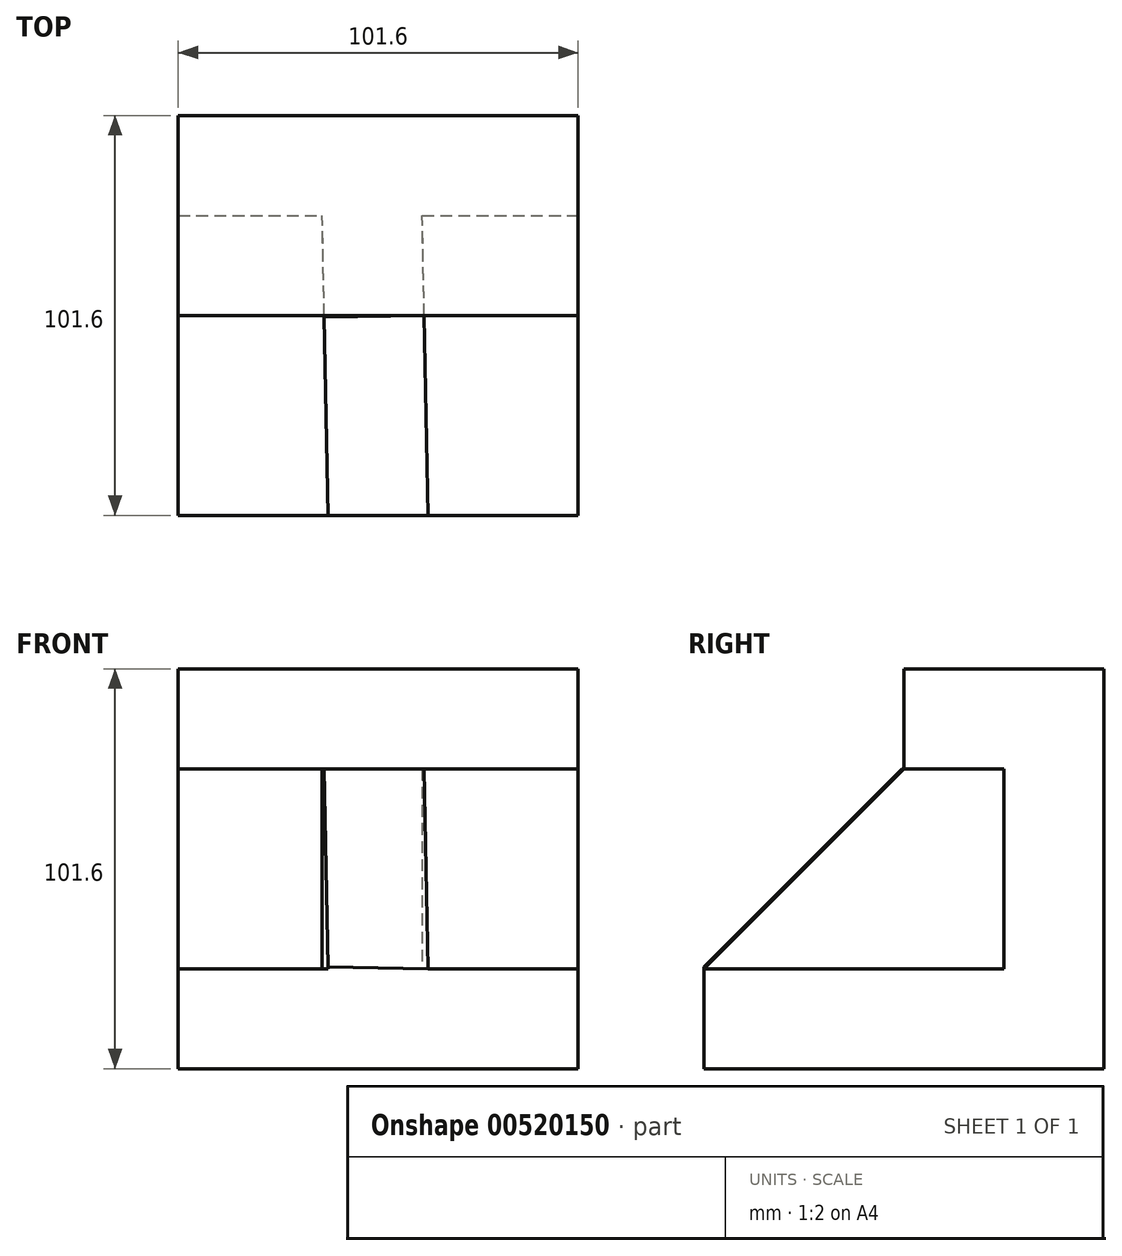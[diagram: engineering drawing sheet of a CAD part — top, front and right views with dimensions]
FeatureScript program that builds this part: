
annotation { "Feature Type Name" : "Feature", "Feature Type Description" : "" }
export const myFeature = defineFeature(function(context is Context, id is Id, definition is map)
    precondition{}
    {
        {
            var Q0;
            Q0=qCreatedBy(makeId("Top.planeOp"),FACE);
            var sketch = newSketch(context, id + "F0", { "sketchPlane" : qUnion([Q0])});
            skLineSegment(sketch, "E0.bottom", {"start": v(-5.75, 0) * mm, "end": v(95.85, 0) * mm});
            skLineSegment(sketch, "E0.top", {"start": v(-5.75, -101.6) * mm, "end": v(95.85, -101.6) * mm});
            skLineSegment(sketch, "E0.left", {"start": v(-5.75, 0) * mm, "end": v(-5.75, -101.6) * mm});
            skLineSegment(sketch, "E0.right", {"start": v(95.85, 0) * mm, "end": v(95.85, -101.6) * mm});
            skSolve(sketch);
        }
        {
            var Q0;
            Q0 = qSketchRegion(id + "F0", true);
            extrude(context, id + "F1", {"entities" : qUnion([Q0]), "depth" : 101.6 * mm, "offsetDistance" : 25.4 * mm});
        }
        {
            var Q0;
            Q0=makeQuery(id+"F1.opExtrude","SWEPT_FACE",FACE,{"disambiguationData":[OSD([sQuery(id+"F0.wireOp",EDGE,"E0.top")])]});
            var sketch = newSketch(context, id + "F2", { "sketchPlane" : qUnion([Q0])});
            skLineSegment(sketch, "E1.bottom", {"start": v(-5.75, 101.6) * mm, "end": v(95.85, 101.6) * mm});
            skLineSegment(sketch, "E1.top", {"start": v(-5.75, 25.4) * mm, "end": v(95.85, 25.4) * mm});
            skLineSegment(sketch, "E1.left", {"start": v(-5.75, 101.6) * mm, "end": v(-5.75, 25.4) * mm});
            skLineSegment(sketch, "E1.right", {"start": v(95.85, 101.6) * mm, "end": v(95.85, 25.4) * mm});
            skSolve(sketch);
        }
        {
            var Q0;
            Q0=makeQuery(id+"F2.imprint","IMPRINT",FACE,{"disambiguationData":[TD([[makeQuery(id+"F2.imprint","IMPRINT",EDGE,{"derivedFrom":sQuery(id+"F2.wireOp",EDGE,"E1.bottom")}),-1.0]])]});
            extrude(context, id + "F3", {"entities" : qUnion([Q0]), "operationType" : NewBodyOperationType.REMOVE, "oppositeDirection" : true, "depth" : 76.2 * mm, "offsetDistance" : 25.4 * mm});
        }
        {
            var Q0;
            Q0=makeQuery(id+"F3.boolean.opBoolean","COPY",FACE,{"derivedFrom":makeQuery(id+"F3.opExtrude","SWEPT_FACE",FACE,{"disambiguationData":[OSD([sQuery(id+"F2.wireOp",EDGE,"E1.top")])]})});
            var sketch = newSketch(context, id + "F4", { "sketchPlane" : qUnion([Q0])});
            skLineSegment(sketch, "E2", {"start": v(-5.75, -101.6) * mm, "end": v(32.35, -101.6) * mm});
            skLineSegment(sketch, "E3", {"start": v(95.85, -101.6) * mm, "end": v(57.75, -101.6) * mm});
            skLineSegment(sketch, "E4", {"start": v(57.75, -101.6) * mm, "end": v(56.25, -25.4) * mm});
            skLineSegment(sketch, "E5", {"start": v(32.35, -101.6) * mm, "end": v(30.85, -25.4) * mm});
            skLineSegment(sketch, "E6", {"start": v(57.75, -101.6) * mm, "end": v(32.35, -101.6) * mm});
            skSolve(sketch);
        }
        {
            var Q0;
            Q0 = qSketchRegion(id + "F4", true);
            var Q1;
            {var subQ0=sQuery(id+"F4.wireOp",EDGE,"E4");Q1=makeQuery(id+"F4.imprint","IMPRINT",FACE,{"disambiguationData":[TD([[makeQuery(id+"F4.imprint","IMPRINT",EDGE,{"derivedFrom":subQ0}),1.0]])]});}
            extrude(context, id + "F5", {"entities" : qUnion([Q0, Q1]), "operationType" : NewBodyOperationType.ADD, "depth" : 50.8 * mm, "offsetDistance" : 25.4 * mm});
        }
        {
            var Q0;
            Q0=makeQuery(id+"F3.boolean.opBoolean","COPY",FACE,{"derivedFrom":makeQuery(id+"F3.opExtrude","CAP_FACE",FACE,{"disambiguationData":[OSD([sQuery(id+"F2.wireOp",EDGE,"E1.bottom"),sQuery(id+"F2.wireOp",EDGE,"E1.top"),sQuery(id+"F2.wireOp",EDGE,"E1.left"),sQuery(id+"F2.wireOp",EDGE,"E1.right")])],"isStart":false})});
            var sketch = newSketch(context, id + "F6", { "sketchPlane" : qUnion([Q0])});
            skLineSegment(sketch, "E7.bottom", {"start": v(-5.75, 101.6) * mm, "end": v(95.85, 101.6) * mm});
            skLineSegment(sketch, "E7.top", {"start": v(-5.75, 76.2) * mm, "end": v(95.85, 76.2) * mm});
            skLineSegment(sketch, "E7.left", {"start": v(-5.75, 101.6) * mm, "end": v(-5.75, 76.2) * mm});
            skLineSegment(sketch, "E7.right", {"start": v(95.85, 101.6) * mm, "end": v(95.85, 76.2) * mm});
            skSolve(sketch);
        }
        {
            var Q0;
            Q0 = qSketchRegion(id + "F6", true);
            extrude(context, id + "F7", {"entities" : qUnion([Q0]), "operationType" : NewBodyOperationType.ADD, "depth" : 25.4 * mm, "offsetDistance" : 25.4 * mm});
        }
        {
            var Q0;
            Q0=makeQuery(id+"F5.opExtrude","SWEPT_FACE",FACE,{"disambiguationData":[OSD([sQuery(id+"F4.wireOp",EDGE,"E4")])]});
            var sketch = newSketch(context, id + "F8", { "sketchPlane" : qUnion([Q0])});
            skLineSegment(sketch, "E8", {"start": v(-26.5, 76.2) * mm, "end": v(-51.9, 76.2) * mm});
            skLineSegment(sketch, "E9", {"start": v(-51.9, 76.2) * mm, "end": v(-102.72, 25.4) * mm});
            skSolve(sketch);
        }
        {
            var Q0;
            Q0=makeQuery(id+"F8.imprint","IMPRINT",FACE,{"disambiguationData":[TD([[makeQuery(id+"F8.imprint","IMPRINT",EDGE,{"derivedFrom":sQuery(id+"F8.wireOp",EDGE,"E9")}),-1.0]])]});
            extrude(context, id + "F9", {"entities" : qUnion([Q0]), "operationType" : NewBodyOperationType.REMOVE, "oppositeDirection" : true, "depth" : 25.4 * mm, "offsetDistance" : 25.4 * mm});
        }
    });
